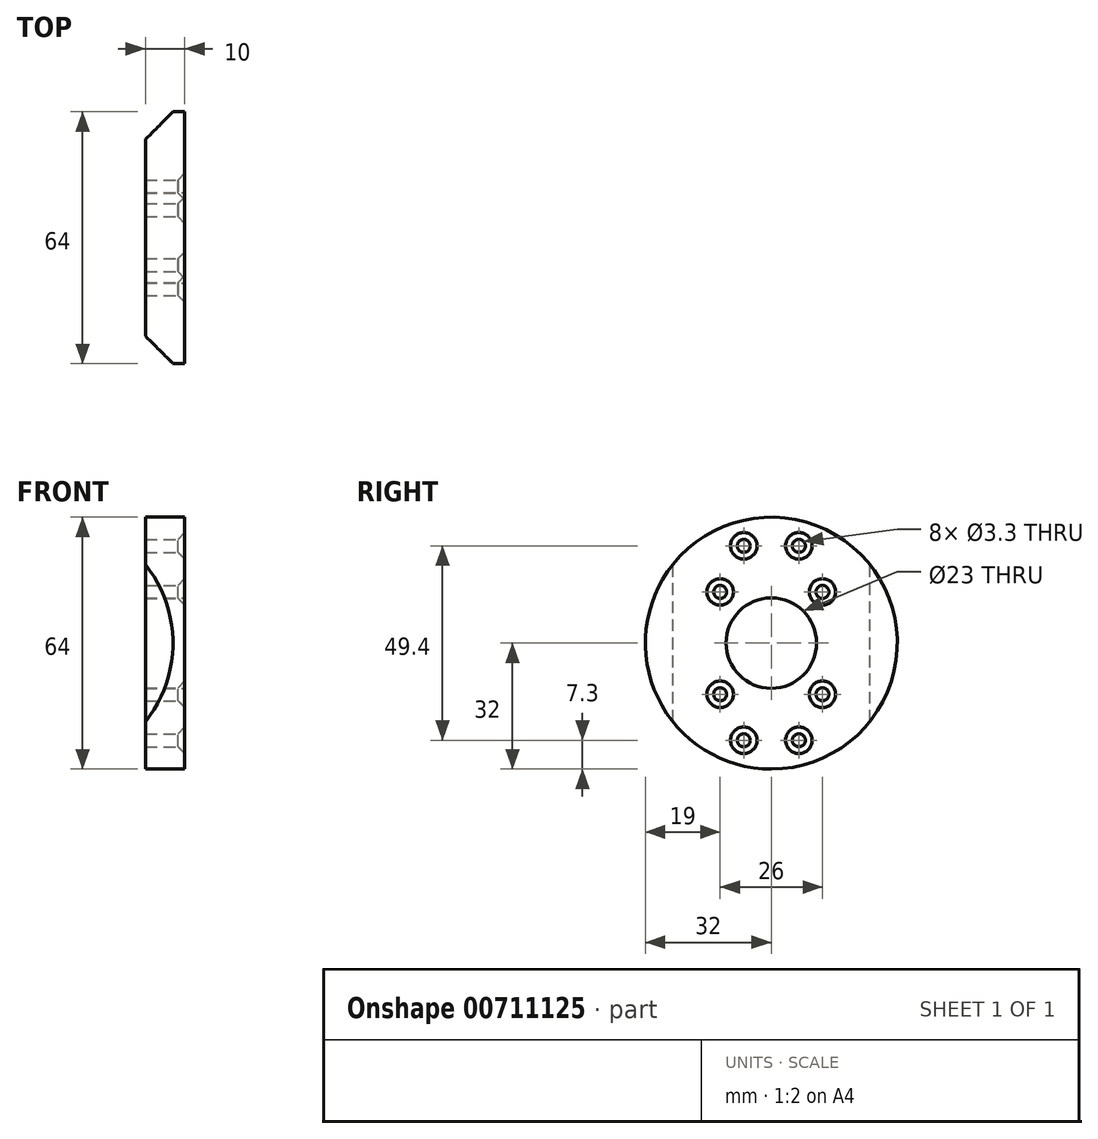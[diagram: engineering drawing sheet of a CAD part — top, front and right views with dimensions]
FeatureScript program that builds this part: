
annotation { "Feature Type Name" : "Feature", "Feature Type Description" : "" }
export const myFeature = defineFeature(function(context is Context, id is Id, definition is map)
    precondition{}
    {
        {
            var Q0;
            Q0=qCreatedBy(makeId("Right.planeOp"),FACE);
            var sketch = newSketch(context, id + "F0", { "sketchPlane" : qUnion([Q0])});
            skCircle(sketch, "E0", {"center": v(0, 0) * mm, "radius": 32 * mm});
            skSolve(sketch);
        }
        {
            var Q0;
            Q0 = qSketchRegion(id + "F0", true);
            extrude(context, id + "F1", {"entities" : qUnion([Q0]), "depth" : 10 * mm, "offsetDistance" : 25 * mm});
        }
        {
            var Q0;
            Q0=makeQuery(id+"F1.opExtrude","CAP_FACE",FACE,{"disambiguationData":[OSD([sQuery(id+"F0.wireOp",EDGE,"E0")])],"isStart":false});
            var sketch = newSketch(context, id + "F2", { "sketchPlane" : qUnion([Q0])});
            skPoint(sketch, "E1", {"position": v(-13, 13) * mm});
            skPoint(sketch, "E2.1.0", {"position": v(-13, -13) * mm});
            skPoint(sketch, "E2.2.0", {"position": v(13, -13) * mm});
            skPoint(sketch, "E2.3.0", {"position": v(13, 13) * mm});
            skPoint(sketch, "E2.center", {"position": v(0, 0) * mm});
            skSolve(sketch);
        }
        {
            var Q0;
            Q0=sQuery(id+"F2.wireOp",VERTEX,"E1");
            var Q1;
            Q1=sQuery(id+"F2.wireOp",VERTEX,"E2.3.0");
            var Q2;
            Q2=sQuery(id+"F2.wireOp",VERTEX,"E2.2.0");
            var Q3;
            Q3=sQuery(id+"F2.wireOp",VERTEX,"E2.1.0");
            var Q4;
            Q4=makeQuery(id+"F1.opExtrude","SWEPT_BODY",BODY,{"disambiguationData":[OSD([sQuery(id+"F0.wireOp",EDGE,"E0")])]});
            hole(context, id + "F3", {"style" : HoleStyle.C_SINK, "endStyle" : HoleEndStyle.THROUGH, "standardTappedOrClearance" : lookupTablePath({ "standard" : "ISO", "fit" : "Normal", "size" : "M3", "type" : "Clearance" }), "standardBlindInLast" : lookupTablePath({ "fit" : "Standard", "standard" : "ISO", "size" : "M3", "type" : "Clearance" }), "holeDiameter" : 3.3 * mm, "cSinkDiameter" : 6.72 * mm, "cSinkAngle" : 90 * degree, "majorDiameter" : 5 * mm, "isTappedThrough" : true, "tappedDepth" : 12 * mm, "tapClearance" : 3, "locations" : qUnion([Q0, Q1, Q2, Q3]), "scope" : qUnion([Q4])});
        }
        {
            var Q0;
            Q0=makeQuery(id+"F1.opExtrude","CAP_FACE",FACE,{"disambiguationData":[OSD([sQuery(id+"F0.wireOp",EDGE,"E0")])],"isStart":false});
            var sketch = newSketch(context, id + "F4", { "sketchPlane" : qUnion([Q0])});
            skPoint(sketch, "E3", {"position": v(-7, 24.7) * mm});
            skLineSegment(sketch, "E4", {"start": v(0, 32) * mm, "end": v(0, -32) * mm, "construction": true});
            skLineSegment(sketch, "E5", {"start": v(-32, 0) * mm, "end": v(32, 0) * mm, "construction": true});
            skPoint(sketch, "E6.MirrorP", {"position": v(7, 24.7) * mm});
            skLineSegment(sketch, "E7.MirrorCS", {"start": v(32, 0) * mm, "end": v(-32, 0) * mm, "construction": true});
            skPoint(sketch, "E8.MirrorP", {"position": v(-7, -24.7) * mm});
            skPoint(sketch, "E9.MirrorP", {"position": v(7, -24.7) * mm});
            skSolve(sketch);
        }
        {
            var Q0;
            Q0=sQuery(id+"F4.wireOp",VERTEX,"E3");
            var Q1;
            Q1=sQuery(id+"F4.wireOp",VERTEX,"E6.MirrorP");
            var Q2;
            Q2=sQuery(id+"F4.wireOp",VERTEX,"E8.MirrorP");
            var Q3;
            Q3=sQuery(id+"F4.wireOp",VERTEX,"E9.MirrorP");
            var Q4;
            Q4=makeQuery(id+"F1.opExtrude","SWEPT_BODY",BODY,{"disambiguationData":[OSD([sQuery(id+"F0.wireOp",EDGE,"E0")])]});
            hole(context, id + "F5", {"style" : HoleStyle.C_SINK, "endStyle" : HoleEndStyle.THROUGH, "standardTappedOrClearance" : lookupTablePath({ "standard" : "ISO", "fit" : "Normal", "size" : "M3", "type" : "Clearance" }), "standardBlindInLast" : lookupTablePath({ "fit" : "Standard", "standard" : "ISO", "size" : "M3", "type" : "Clearance" }), "holeDiameter" : 3.3 * mm, "cSinkDiameter" : 6.72 * mm, "cSinkAngle" : 90 * degree, "majorDiameter" : 5 * mm, "isTappedThrough" : true, "tappedDepth" : 12 * mm, "tapClearance" : 3, "locations" : qUnion([Q0, Q1, Q2, Q3]), "scope" : qUnion([Q4])});
        }
        {
            var Q0;
            Q0=makeQuery(id+"F1.opExtrude","CAP_FACE",FACE,{"disambiguationData":[OSD([sQuery(id+"F0.wireOp",EDGE,"E0")])],"isStart":false});
            var sketch = newSketch(context, id + "F6", { "sketchPlane" : qUnion([Q0])});
            skCircle(sketch, "E10", {"center": v(0, 0) * mm, "radius": 11.5 * mm});
            skSolve(sketch);
        }
        {
            var Q0;
            Q0 = qSketchRegion(id + "F6", true);
            extrude(context, id + "F7", {"entities" : qUnion([Q0]), "operationType" : NewBodyOperationType.REMOVE, "endBound" : BoundingType.THROUGH_ALL, "oppositeDirection" : true, "depth" : 25 * mm, "offsetDistance" : 25 * mm});
        }
        {
            var Q0;
            Q0=qCreatedBy(makeId("Top.planeOp"),FACE);
            var sketch = newSketch(context, id + "F8", { "sketchPlane" : qUnion([Q0])});
            skLineSegment(sketch, "E11", {"start": v(0, 0) * mm, "end": v(0, -32) * mm, "construction": true});
            skLineSegment(sketch, "E12", {"start": v(0, -32) * mm, "end": v(7, -32) * mm});
            skLineSegment(sketch, "E13", {"start": v(7, -32) * mm, "end": v(0, -25) * mm});
            skLineSegment(sketch, "E14", {"start": v(0, -25) * mm, "end": v(0, -32) * mm});
            skLineSegment(sketch, "E15", {"start": v(0, 0) * mm, "end": v(10.08, 0) * mm, "construction": true});
            skLineSegment(sketch, "E16.MirrorCS", {"start": v(0, 25) * mm, "end": v(0, 32) * mm});
            skLineSegment(sketch, "E17.MirrorCS", {"start": v(7, 32) * mm, "end": v(0, 25) * mm});
            skLineSegment(sketch, "E18.MirrorCS", {"start": v(0, 0) * mm, "end": v(0, 32) * mm, "construction": true});
            skLineSegment(sketch, "E19.MirrorCS", {"start": v(0, 32) * mm, "end": v(7, 32) * mm});
            skSolve(sketch);
        }
        {
            var Q0;
            Q0 = qSketchRegion(id + "F8", true);
            extrude(context, id + "F9", {"entities" : qUnion([Q0]), "operationType" : NewBodyOperationType.REMOVE, "endBound" : BoundingType.THROUGH_ALL, "oppositeDirection" : true, "depth" : 25 * mm, "offsetDistance" : 25 * mm, "hasSecondDirection" : true, "secondDirectionBound" : SecondDirectionBoundingType.THROUGH_ALL, "secondDirectionOppositeDirection" : false, "secondDirectionDepth" : 25 * mm});
        }
    });
